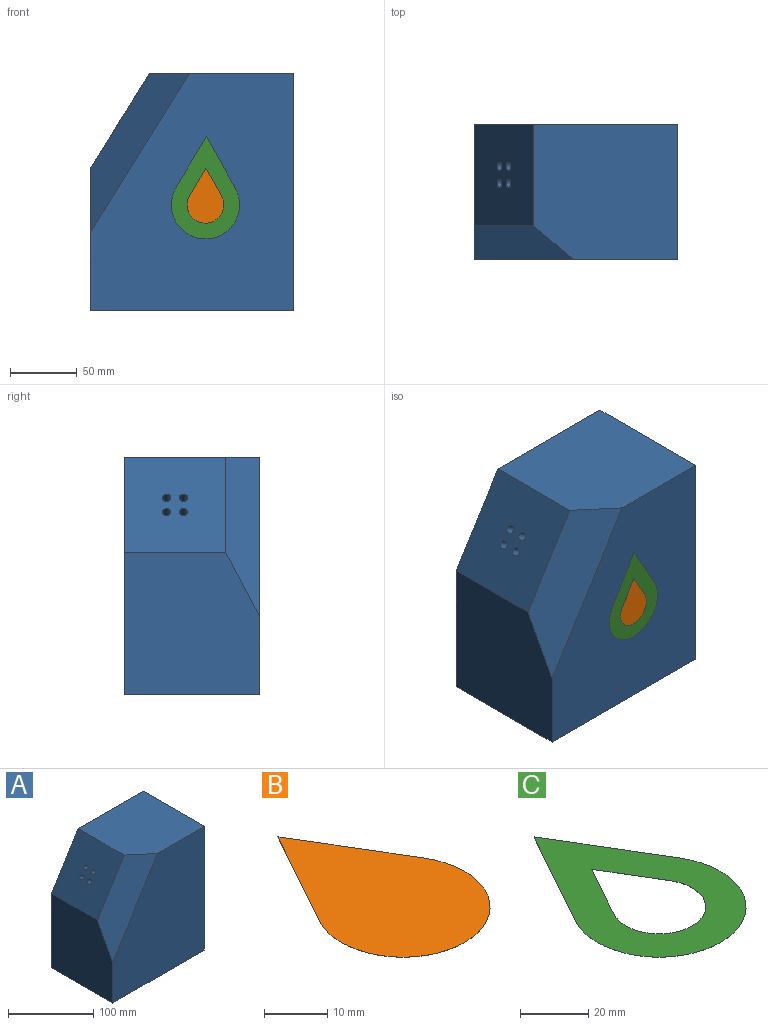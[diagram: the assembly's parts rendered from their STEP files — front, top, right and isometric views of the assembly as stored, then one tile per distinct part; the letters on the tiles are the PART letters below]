
ASSEMBLY  parts=3 mates=2
PART A: 16 faces, bbox 152.4x101.6x177.8 mm
  f0: plane 177.8x101.6mm, normal (1,0,0), area 18064.5mm2, adj f1,f3,f4,f5
  f1: plane 152.4x101.6mm, normal (0,0,-1), area 15483.8mm2, adj f0,f2,f4,f5
  f2: plane 106.47x101.6mm, normal (-1,0,0), area 10206.3mm2, adj f1,f4,f5,f6,f7
  f3: plane 108.04x101.6mm, normal (0,0,1), area 10597.1mm2, adj f0,f4,f5,f6,f7
  f4: plane 177.8x152.4mm, normal (0,-1,0), area 22661.6mm2, adj f0,f1,f2,f3,f7
  f5: plane 177.8x152.4mm, normal (0,1,0), area 25514.6mm2, adj f0,f1,f2,f3,f6
  f6: plane 76.2x71.33mm, normal (-0.85,0,0.53), area 6274.2mm2, adj f2,f3,f5,f7,f8,f10,f12,f14
  f7: plane 119.43x74.27mm, normal (-0.6,-0.71,0.37), area 4034.7mm2, adj f2,f3,f4,f6
  f8: cylinder r=3.17mm len=24.92mm, axis (-0.85,0,0.53), area 506.7mm2, adj f6,f9
  f9: plane 6.35x5.39mm, normal (-0.85,0,0.53), area 31.7mm2, adj f8
  f10: cylinder r=3.17mm len=24.92mm, axis (-0.85,0,0.53), area 506.7mm2, adj f6,f11
  f11: plane 6.35x5.39mm, normal (-0.85,0,0.53), area 31.7mm2, adj f10
  f12: cylinder r=3.17mm len=24.92mm, axis (-0.85,0,0.53), area 506.7mm2, adj f6,f13
  f13: plane 6.35x5.39mm, normal (-0.85,0,0.53), area 31.7mm2, adj f12
  f14: cylinder r=3.17mm len=24.92mm, axis (-0.85,0,0.53), area 506.7mm2, adj f6,f15
  f15: plane 6.35x5.39mm, normal (-0.85,0,0.53), area 31.7mm2, adj f14
PART B: 5 faces, bbox 27.5x41.2x0 mm
  f0: plane 20.8x11.59mm, normal (-0.87,0.49,0), area 0.5mm2, adj f1,f2,f3,f4
  f1: cylinder r=13.75mm len=27.49mm, axis (0,0,-1), area 1.3mm2, adj f0,f2,f3,f4
  f2: plane 20.44x12.22mm, normal (0.86,0.51,0), area 0.5mm2, adj f0,f1,f3,f4
  f3: plane 41.24x27.49mm, normal (0,0,1), area 723.1mm2, adj f0,f1,f2
  f4: plane 41.24x27.49mm, normal (0,0,-1), area 723.1mm2, adj f0,f1,f2
PART C: 8 faces, bbox 51.2x76.8x0 mm
  f0: plane 38.73x21.58mm, normal (-0.87,0.49,0), area 1mm2, adj f1,f5,f6,f7
  f1: cylinder r=25.6mm len=51.2mm, axis (0,0,-1), area 2.4mm2, adj f0,f5,f6,f7
  f2: cylinder r=13.75mm len=27.49mm, axis (0,0,-1), area 1.3mm2, adj f3,f4,f6,f7
  f3: plane 20.8x11.59mm, normal (0.87,-0.49,0), area 0.5mm2, adj f2,f4,f6,f7
  f4: plane 20.44x12.22mm, normal (-0.86,-0.51,0), area 0.5mm2, adj f2,f3,f6,f7
  f5: plane 38.06x22.75mm, normal (0.86,0.51,0), area 1mm2, adj f0,f1,f6,f7
  f6: plane 76.79x51.2mm, normal (0,0,1), area 1784.6mm2, adj f0,f1,f2,f3,f4,f5
  f7: plane 76.79x51.2mm, normal (0,0,-1), area 1784.6mm2, adj f0,f1,f2,f3,f4,f5
PLACE A t=(35.11,-56.56,33.29)mm
PLACE B rot(axis=(0,-0.71,-0.71),180deg) t=(-31.02,-158.18,112.58)mm
PLACE C rot(axis=(0,-0.71,-0.71),180deg) t=(-31.02,-158.18,112.58)mm
MATE fastened C.f1 <-> A.f4  axis (0,1,0) through (-31.02,-158.16,112.58)mm
MATE fastened B.f1 <-> A.f4  axis (0,1,0) through (-31.02,-158.16,112.58)mm
